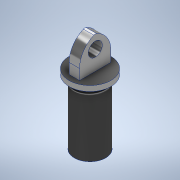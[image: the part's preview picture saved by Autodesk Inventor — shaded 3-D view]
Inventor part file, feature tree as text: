
AUTODESK INVENTOR PART (.ipt)
format: ipt  version: 2020 (Build 240168000, 168)  size: 153,088 bytes
history: native  units: mm
features: sketch x2, extrude x2, revolve x1, fillet x1, thread x1
ambient origin geometry x8: Origin, YZ Plane, XZ Plane, XY Plane, X Axis, Y Axis, Z Axis, Center Point
bodies: Solid1 (feature_tree)
feature tree (7):
  sketch  "Sketch1"  dims[d0=100.0mm d1=30.0mm]
  revolve  "Revolution1"  [1 undecoded]
  extrude  "Extrusion1"  Depth=33.75mm
  fillet  "Fillet1"  Radius=22.5mm
  thread  "Thread1"  [1 undecoded]
  extrude  "Extrusion2"  Depth=33.75mm
  sketch  "Sketch2"  dims[d2=7.5mm d3=7.6mm d9=22.5mm d10=15.0mm d11=22.5mm d15=20.0mm d16=90.0deg d18=15.0mm d19=0.0mm d20=5.0mm d21=10.0mm d22=0.0mm d23=20.0mm d24=75.0mm d25=0.0mm d26=33.75mm d27=33.75mm]
note: 2 required parameter values undecoded (feature->parameter linkage not recoverable at this tier; creation-order binding heuristic only, values carry confidence <= 0.55)